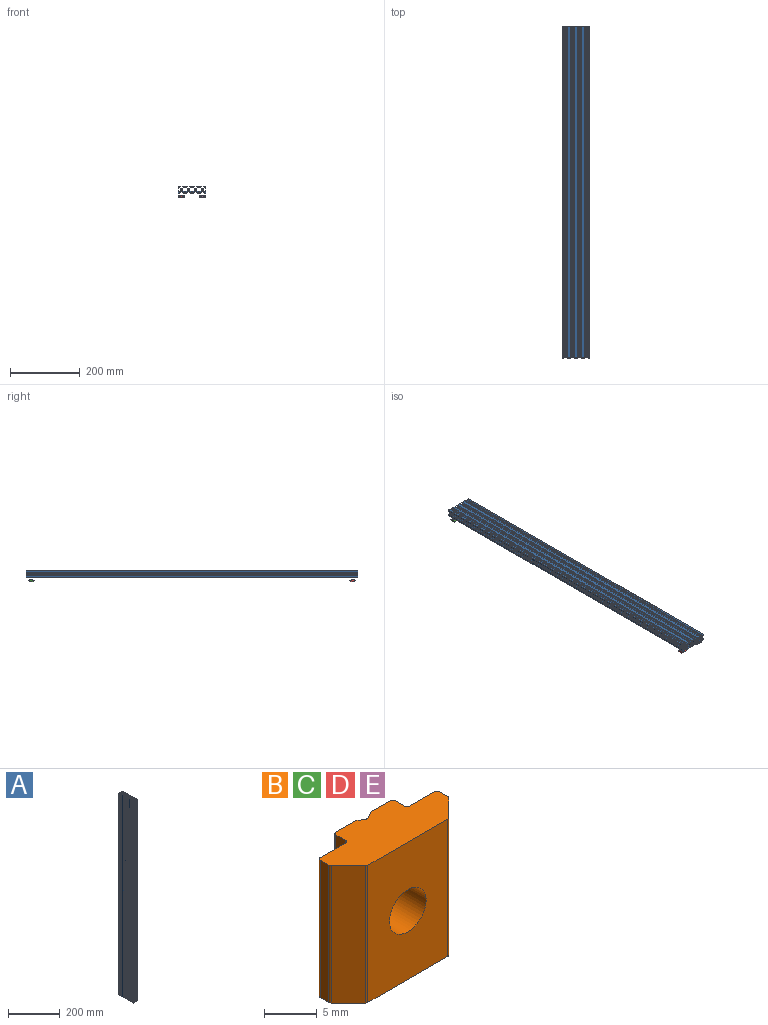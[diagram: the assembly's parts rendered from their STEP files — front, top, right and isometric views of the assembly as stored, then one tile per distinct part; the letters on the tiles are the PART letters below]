
ASSEMBLY  parts=5 mates=7
PART A: 240 faces, bbox 20x80x949 mm
  f0: plane 913.01x0.21mm, normal (0.71,0.71,0), area 271.1mm2, adj f2,f32,f234,f235
  f1: plane 12.01x0.21mm, normal (0.71,0.71,0), area 3.6mm2, adj f3,f33,f232,f234
  f2: plane 913.01x0.21mm, normal (0.71,-0.71,0), area 271.1mm2, adj f0,f4,f234,f235
  f3: plane 12.01x0.21mm, normal (0.71,-0.71,0), area 3.6mm2, adj f1,f5,f232,f234
  f4: plane 917.06x2.63mm, normal (1,0,0), area 2403.7mm2, adj f2,f48,f234,f235
  f5: plane 14.03x2.63mm, normal (1,0,0), area 33.1mm2, adj f3,f48,f232,f234
  f6: plane 917.06x2.63mm, normal (-1,0,0), area 2403.7mm2, adj f9,f77,f234,f235
  f7: plane 14.03x2.63mm, normal (-1,0,0), area 33.1mm2, adj f77,f79,f232,f234
  f8: plane 12.01x0.21mm, normal (-0.71,-0.71,0), area 3.6mm2, adj f10,f78,f233,f235
  f9: plane 913.01x0.21mm, normal (-0.71,-0.71,0), area 271.1mm2, adj f6,f11,f234,f235
  f10: plane 12.01x0.21mm, normal (-0.71,0.71,0), area 3.6mm2, adj f8,f81,f233,f235
  f11: plane 913.01x0.21mm, normal (-0.71,0.71,0), area 271.1mm2, adj f9,f12,f234,f235
  f12: plane 917.06x2.63mm, normal (-1,0,0), area 2403.7mm2, adj f11,f82,f234,f235
  f13: plane 14.03x2.63mm, normal (-1,0,0), area 33.1mm2, adj f80,f82,f232,f234
  f14: plane 14.03x2.63mm, normal (-1,0,0), area 33.1mm2, adj f122,f124,f232,f239
  f15: plane 917.06x2.63mm, normal (-1,0,0), area 2403.7mm2, adj f16,f122,f237,f239
  f16: plane 913.01x0.21mm, normal (-0.71,-0.71,0), area 271.1mm2, adj f15,f18,f237,f239
  f17: plane 12.01x0.21mm, normal (-0.71,-0.71,0), area 3.6mm2, adj f19,f123,f233,f237
  f18: plane 913.01x0.21mm, normal (-0.71,0.71,0), area 271.1mm2, adj f16,f21,f237,f239
  f19: plane 12.01x0.21mm, normal (-0.71,0.71,0), area 3.6mm2, adj f17,f126,f233,f237
  f20: plane 14.03x2.63mm, normal (-1,0,0), area 33.1mm2, adj f125,f127,f232,f239
  f21: plane 917.06x2.63mm, normal (-1,0,0), area 2403.7mm2, adj f18,f127,f237,f239
  f22: plane 14.03x2.63mm, normal (1,0,0), area 33.1mm2, adj f24,f156,f232,f239
  f23: plane 917.06x2.63mm, normal (1,0,0), area 2403.7mm2, adj f25,f156,f237,f239
  f24: plane 12.01x0.21mm, normal (0.71,0.71,0), area 3.6mm2, adj f22,f26,f232,f239
  f25: plane 913.01x0.21mm, normal (0.71,0.71,0), area 271.1mm2, adj f23,f27,f237,f239
  f26: plane 12.01x0.21mm, normal (0.71,-0.71,0), area 3.6mm2, adj f24,f28,f232,f239
  f27: plane 913.01x0.21mm, normal (0.71,-0.71,0), area 271.1mm2, adj f25,f29,f237,f239
  f28: plane 14.03x2.63mm, normal (1,0,0), area 33.1mm2, adj f26,f161,f232,f239
  f29: plane 917.06x2.63mm, normal (1,0,0), area 2403.7mm2, adj f27,f161,f237,f239
  f30: cylinder r=2.1mm len=12.86mm, axis (0,0,-1), area 163.8mm2, adj f232,f239
  f31: cylinder r=2.1mm len=12.86mm, axis (0,0,-1), area 163.8mm2, adj f232,f234
  f32: plane 917.06x2.63mm, normal (1,0,0), area 2403.7mm2, adj f0,f201,f234,f235
  f33: plane 14.03x2.63mm, normal (1,0,0), area 33.1mm2, adj f1,f201,f232,f234
  f34: plane 949x3.4mm, normal (0.71,-0.71,0), area 4563.1mm2, adj f35,f231,f232,f233
  f35: plane 949x5.68mm, normal (0,-1,0), area 5389.1mm2, adj f34,f36,f232,f233
  f36: plane 949x3.4mm, normal (-0.71,-0.71,0), area 4563.1mm2, adj f35,f37,f232,f233
  f37: plane 949x1.96mm, normal (0,-1,0), area 1860.7mm2, adj f36,f38,f232,f233
  f38: plane 949x5.4mm, normal (-1,0,0), area 5124.6mm2, adj f37,f39,f232,f233
  f39: plane 949x1.96mm, normal (0,1,0), area 1860.7mm2, adj f38,f40,f232,f233
  f40: plane 949x3.4mm, normal (-0.71,0.71,0), area 4563.1mm2, adj f39,f41,f232,f233
  f41: plane 949x5.68mm, normal (0,1,0), area 5389.1mm2, adj f40,f42,f232,f233
  f42: plane 949x3.4mm, normal (0.71,0.71,0), area 4563.1mm2, adj f41,f43,f232,f233
  f43: plane 949x1.96mm, normal (0,1,0), area 1860.7mm2, adj f42,f44,f232,f233
  f44: plane 949x5.4mm, normal (1,0,0), area 5124.6mm2, adj f43,f231,f232,f233
  f45: plane 12.01x0.21mm, normal (0.71,0.71,0), area 3.6mm2, adj f46,f228,f233,f235
  f46: plane 12.01x0.21mm, normal (0.71,-0.71,0), area 3.6mm2, adj f45,f47,f233,f235
  f47: plane 14.03x2.63mm, normal (1,0,0), area 33.1mm2, adj f46,f48,f233,f235
  f48: plane 949x2.66mm, normal (0.71,-0.71,0), area 3570.3mm2, adj f4,f5,f47,f49,f232,f233,f234,f235
  f49: plane 949x1.64mm, normal (0,-1,0), area 1555.7mm2, adj f48,f50,f232,f233
  f50: plane 949x2.38mm, normal (-1,0,0), area 2253.9mm2, adj f49,f51,f232,f233
  f51: plane 949x0.35mm, normal (0,-1,0), area 327.4mm2, adj f50,f52,f232,f233
  f52: plane 949x1.46mm, normal (0.71,-0.71,0), area 1952.7mm2, adj f51,f53,f232,f233
  f53: plane 949x4.92mm, normal (1,0,0), area 4669.1mm2, adj f52,f54,f232,f233
  f54: cylinder r=0.5mm len=949mm, axis (0,0,-1), area 745.3mm2, adj f53,f55,f232,f233
  f55: plane 949x4.92mm, normal (0,1,0), area 4669.1mm2, adj f54,f56,f232,f233
  f56: plane 949x1.46mm, normal (-0.71,0.71,0), area 1952.7mm2, adj f55,f57,f232,f233
  f57: plane 949x0.35mm, normal (-1,0,0), area 327.4mm2, adj f56,f58,f232,f233
  f58: plane 949x2.38mm, normal (0,-1,0), area 2253.9mm2, adj f57,f59,f232,f233
  f59: plane 949x1.64mm, normal (-1,0,0), area 1555.7mm2, adj f58,f60,f232,f233
  f60: plane 949x2.66mm, normal (-0.71,0.71,0), area 3570.8mm2, adj f59,f61,f232,f233
  f61: plane 949x2.63mm, normal (0,1,0), area 2495.2mm2, adj f60,f62,f232,f233
  f62: plane 949x0.21mm, normal (-0.71,0.71,0), area 281.8mm2, adj f61,f63,f232,f233
  f63: plane 949x0.21mm, normal (0.71,0.71,0), area 281.8mm2, adj f62,f64,f232,f233
  f64: plane 949x2.63mm, normal (0,1,0), area 2495.2mm2, adj f63,f65,f232,f233
  f65: plane 949x2.66mm, normal (0.71,0.71,0), area 3570.8mm2, adj f64,f66,f232,f233
  f66: plane 949x1.64mm, normal (1,0,0), area 1555.7mm2, adj f65,f67,f232,f233
  f67: plane 949x2.38mm, normal (0,-1,0), area 2253.9mm2, adj f66,f68,f232,f233
  f68: plane 949x0.35mm, normal (1,0,0), area 327.4mm2, adj f67,f69,f232,f233
  f69: plane 949x1.46mm, normal (0.71,0.71,0), area 1952.7mm2, adj f68,f70,f232,f233
  f70: plane 949x4.92mm, normal (0,1,0), area 4669.1mm2, adj f69,f71,f232,f233
  f71: cylinder r=0.5mm len=949mm, axis (0,0,-1), area 745.3mm2, adj f70,f72,f232,f233
  f72: plane 949x4.92mm, normal (-1,0,0), area 4669.1mm2, adj f71,f73,f232,f233
  f73: plane 949x1.46mm, normal (-0.71,-0.71,0), area 1952.7mm2, adj f72,f74,f232,f233
  f74: plane 949x0.35mm, normal (0,-1,0), area 327.4mm2, adj f73,f75,f232,f233
  f75: plane 949x2.38mm, normal (1,0,0), area 2253.9mm2, adj f74,f76,f232,f233
  f76: plane 949x1.64mm, normal (0,-1,0), area 1555.7mm2, adj f75,f77,f232,f233
  f77: plane 949x2.66mm, normal (-0.71,-0.71,0), area 3570.3mm2, adj f6,f7,f76,f78,f232,f233,f234,f235
  f78: plane 14.03x2.63mm, normal (-1,0,0), area 33.1mm2, adj f8,f77,f233,f235
  f79: plane 12.01x0.21mm, normal (-0.71,-0.71,0), area 3.6mm2, adj f7,f80,f232,f234
  f80: plane 12.01x0.21mm, normal (-0.71,0.71,0), area 3.6mm2, adj f13,f79,f232,f234
  f81: plane 14.03x2.63mm, normal (-1,0,0), area 33.1mm2, adj f10,f82,f233,f235
  f82: plane 949x2.66mm, normal (-0.71,0.71,0), area 3570.3mm2, adj f12,f13,f81,f83,f232,f233,f234,f235
  f83: plane 949x1.64mm, normal (0,1,0), area 1555.7mm2, adj f82,f84,f232,f233
  f84: plane 949x2.38mm, normal (1,0,0), area 2253.9mm2, adj f83,f85,f232,f233
  f85: plane 949x0.35mm, normal (0,1,0), area 327.4mm2, adj f84,f86,f232,f233
  f86: plane 949x1.46mm, normal (-0.71,0.71,0), area 1952.7mm2, adj f85,f87,f232,f233
  f87: plane 949x10.84mm, normal (-1,0,0), area 10287.2mm2, adj f86,f88,f232,f233
  f88: plane 949x1.46mm, normal (-0.71,-0.71,0), area 1952.7mm2, adj f87,f89,f232,f233
  f89: plane 949x0.35mm, normal (0,-1,0), area 327.4mm2, adj f88,f90,f232,f233
  f90: plane 949x2.38mm, normal (1,0,0), area 2253.9mm2, adj f89,f91,f232,f233
  f91: plane 949x1.64mm, normal (0,-1,0), area 1555.7mm2, adj f90,f92,f232,f233
  f92: plane 949x2.66mm, normal (-0.71,-0.71,0), area 3570.8mm2, adj f91,f93,f232,f233
  f93: plane 949x2.63mm, normal (-1,0,0), area 2495.2mm2, adj f92,f94,f232,f233
  f94: plane 949x0.21mm, normal (-0.71,-0.71,0), area 281.8mm2, adj f93,f95,f232,f233
  f95: plane 949x0.21mm, normal (-0.71,0.71,0), area 281.8mm2, adj f94,f96,f232,f233
  f96: plane 949x2.63mm, normal (-1,0,0), area 2495.2mm2, adj f95,f97,f232,f233
  f97: plane 949x2.66mm, normal (-0.71,0.71,0), area 3570.8mm2, adj f96,f98,f232,f233
  f98: plane 949x1.64mm, normal (0,1,0), area 1555.7mm2, adj f97,f99,f232,f233
  f99: plane 949x2.38mm, normal (1,0,0), area 2253.9mm2, adj f98,f100,f232,f233
  f100: plane 949x0.35mm, normal (0,1,0), area 327.4mm2, adj f99,f101,f232,f233
  f101: plane 949x1.46mm, normal (-0.71,0.71,0), area 1952.7mm2, adj f100,f102,f232,f233
  f102: plane 949x10.84mm, normal (-1,0,0), area 10287.2mm2, adj f101,f103,f232,f233
  f103: plane 949x1.46mm, normal (-0.71,-0.71,0), area 1952.7mm2, adj f102,f104,f232,f233
  f104: plane 949x0.35mm, normal (0,-1,0), area 327.4mm2, adj f103,f105,f232,f233
  f105: plane 949x2.38mm, normal (1,0,0), area 2253.9mm2, adj f104,f106,f232,f233
  f106: plane 949x1.64mm, normal (0,-1,0), area 1555.7mm2, adj f105,f107,f232,f233
  f107: plane 949x2.66mm, normal (-0.71,-0.71,0), area 3570.8mm2, adj f106,f108,f232,f233
  f108: plane 949x2.63mm, normal (-1,0,0), area 2495.2mm2, adj f107,f109,f232,f233
  f109: plane 949x0.21mm, normal (-0.71,-0.71,0), area 281.8mm2, adj f108,f110,f232,f233
  f110: plane 949x0.21mm, normal (-0.71,0.71,0), area 281.8mm2, adj f109,f111,f232,f233
  f111: plane 949x2.63mm, normal (-1,0,0), area 2495.2mm2, adj f110,f112,f232,f233
  f112: plane 949x2.66mm, normal (-0.71,0.71,0), area 3570.8mm2, adj f111,f113,f232,f233
  f113: plane 949x1.64mm, normal (0,1,0), area 1555.7mm2, adj f112,f114,f232,f233
  f114: plane 949x2.38mm, normal (1,0,0), area 2253.9mm2, adj f113,f115,f232,f233
  f115: plane 949x0.35mm, normal (0,1,0), area 327.4mm2, adj f114,f116,f232,f233
  f116: plane 949x1.46mm, normal (-0.71,0.71,0), area 1952.7mm2, adj f115,f117,f232,f233
  f117: plane 949x10.84mm, normal (-1,0,0), area 10287.2mm2, adj f116,f118,f232,f233
  f118: plane 949x1.46mm, normal (-0.71,-0.71,0), area 1952.7mm2, adj f117,f119,f232,f233
  f119: plane 949x0.35mm, normal (0,-1,0), area 327.4mm2, adj f118,f120,f232,f233
  f120: plane 949x2.38mm, normal (1,0,0), area 2253.9mm2, adj f119,f121,f232,f233
  f121: plane 949x1.64mm, normal (0,-1,0), area 1555.7mm2, adj f120,f122,f232,f233
  f122: plane 949x2.66mm, normal (-0.71,-0.71,0), area 3570.3mm2, adj f14,f15,f121,f123,f232,f233,f237,f239
  f123: plane 14.03x2.63mm, normal (-1,0,0), area 33.1mm2, adj f17,f122,f233,f237
  f124: plane 12.01x0.21mm, normal (-0.71,-0.71,0), area 3.6mm2, adj f14,f125,f232,f239
  f125: plane 12.01x0.21mm, normal (-0.71,0.71,0), area 3.6mm2, adj f20,f124,f232,f239
  f126: plane 14.03x2.63mm, normal (-1,0,0), area 33.1mm2, adj f19,f127,f233,f237
  f127: plane 949x2.66mm, normal (-0.71,0.71,0), area 3570.3mm2, adj f20,f21,f126,f128,f232,f233,f237,f239
  f128: plane 949x1.64mm, normal (0,1,0), area 1555.7mm2, adj f127,f129,f232,f233
  f129: plane 949x2.38mm, normal (1,0,0), area 2253.9mm2, adj f128,f130,f232,f233
  f130: plane 949x0.35mm, normal (0,1,0), area 327.4mm2, adj f129,f131,f232,f233
  f131: plane 949x1.46mm, normal (-0.71,0.71,0), area 1952.7mm2, adj f130,f132,f232,f233
  f132: plane 949x4.92mm, normal (-1,0,0), area 4669.1mm2, adj f131,f133,f232,f233
  f133: cylinder r=0.5mm len=949mm, axis (0,0,-1), area 745.3mm2, adj f132,f134,f232,f233
  f134: plane 949x4.92mm, normal (0,-1,0), area 4669.1mm2, adj f133,f135,f232,f233
  f135: plane 949x1.46mm, normal (0.71,-0.71,0), area 1952.7mm2, adj f134,f136,f232,f233
  f136: plane 949x0.35mm, normal (1,0,0), area 327.4mm2, adj f135,f137,f232,f233
  f137: plane 949x2.38mm, normal (0,1,0), area 2253.9mm2, adj f136,f138,f232,f233
  f138: plane 949x1.64mm, normal (1,0,0), area 1555.7mm2, adj f137,f139,f232,f233
  f139: plane 949x2.66mm, normal (0.71,-0.71,0), area 3570.8mm2, adj f138,f140,f232,f233
  f140: plane 949x2.63mm, normal (0,-1,0), area 2495.2mm2, adj f139,f141,f232,f233
  f141: plane 949x0.21mm, normal (0.71,-0.71,0), area 281.8mm2, adj f140,f142,f232,f233
  f142: plane 949x0.21mm, normal (-0.71,-0.71,0), area 281.8mm2, adj f141,f143,f232,f233
  f143: plane 949x2.63mm, normal (0,-1,0), area 2495.2mm2, adj f142,f144,f232,f233
  f144: plane 949x2.66mm, normal (-0.71,-0.71,0), area 3570.8mm2, adj f143,f145,f232,f233
  f145: plane 949x1.64mm, normal (-1,0,0), area 1555.7mm2, adj f144,f146,f232,f233
  f146: plane 949x2.38mm, normal (0,1,0), area 2253.9mm2, adj f145,f147,f232,f233
  f147: plane 949x0.35mm, normal (-1,0,0), area 327.4mm2, adj f146,f148,f232,f233
  f148: plane 949x1.46mm, normal (-0.71,-0.71,0), area 1952.7mm2, adj f147,f149,f232,f233
  f149: plane 949x4.92mm, normal (0,-1,0), area 4669.1mm2, adj f148,f150,f232,f233
  f150: cylinder r=0.5mm len=949mm, axis (0,0,-1), area 745.3mm2, adj f149,f151,f232,f233
  f151: plane 949x4.92mm, normal (1,0,0), area 4669.1mm2, adj f150,f152,f232,f233
  f152: plane 949x1.46mm, normal (0.71,0.71,0), area 1952.7mm2, adj f151,f153,f232,f233
  f153: plane 949x0.35mm, normal (0,1,0), area 327.4mm2, adj f152,f154,f232,f233
  f154: plane 949x2.38mm, normal (-1,0,0), area 2253.9mm2, adj f153,f155,f232,f233
  f155: plane 949x1.64mm, normal (0,1,0), area 1555.7mm2, adj f154,f156,f232,f233
  f156: plane 949x2.66mm, normal (0.71,0.71,0), area 3570.3mm2, adj f22,f23,f155,f157,f232,f233,f237,f239
  f157: plane 14.03x2.63mm, normal (1,0,0), area 33.1mm2, adj f156,f158,f233,f237
  f158: plane 12.01x0.21mm, normal (0.71,0.71,0), area 3.6mm2, adj f157,f159,f233,f237
  f159: plane 12.01x0.21mm, normal (0.71,-0.71,0), area 3.6mm2, adj f158,f160,f233,f237
  f160: plane 14.03x2.63mm, normal (1,0,0), area 33.1mm2, adj f159,f161,f233,f237
  f161: plane 949x2.66mm, normal (0.71,-0.71,0), area 3570.3mm2, adj f28,f29,f160,f162,f232,f233,f237,f239
  f162: plane 949x1.64mm, normal (0,-1,0), area 1555.7mm2, adj f161,f163,f232,f233
  f163: plane 949x2.38mm, normal (-1,0,0), area 2253.9mm2, adj f162,f164,f232,f233
  f164: plane 949x0.35mm, normal (0,-1,0), area 327.4mm2, adj f163,f165,f232,f233
  f165: plane 949x1.46mm, normal (0.71,-0.71,0), area 1952.7mm2, adj f164,f166,f232,f233
  f166: plane 949x10.84mm, normal (1,0,0), area 10287.2mm2, adj f165,f167,f232,f233
  f167: plane 949x1.46mm, normal (0.71,0.71,0), area 1952.7mm2, adj f166,f168,f232,f233
  f168: plane 949x0.35mm, normal (0,1,0), area 327.4mm2, adj f167,f169,f232,f233
  f169: plane 949x2.38mm, normal (-1,0,0), area 2253.9mm2, adj f168,f170,f232,f233
  f170: plane 949x1.64mm, normal (0,1,0), area 1555.7mm2, adj f169,f171,f232,f233
  f171: plane 949x2.66mm, normal (0.71,0.71,0), area 3570.8mm2, adj f170,f172,f232,f233
  f172: plane 949x2.63mm, normal (1,0,0), area 2495.2mm2, adj f171,f173,f232,f233
  f173: plane 949x0.21mm, normal (0.71,0.71,0), area 281.8mm2, adj f172,f174,f232,f233
  f174: plane 949x0.21mm, normal (0.71,-0.71,0), area 281.8mm2, adj f173,f175,f232,f233
  f175: plane 949x2.63mm, normal (1,0,0), area 2495.2mm2, adj f174,f176,f232,f233
  f176: plane 949x2.66mm, normal (0.71,-0.71,0), area 3570.8mm2, adj f175,f177,f232,f233
  f177: plane 949x1.64mm, normal (0,-1,0), area 1555.7mm2, adj f176,f178,f232,f233
  f178: plane 949x2.38mm, normal (-1,0,0), area 2253.9mm2, adj f177,f179,f232,f233
  f179: plane 949x0.35mm, normal (0,-1,0), area 327.4mm2, adj f178,f180,f232,f233
  f180: plane 949x1.46mm, normal (0.71,-0.71,0), area 1952.7mm2, adj f179,f181,f232,f233
  f181: plane 949x10.84mm, normal (1,0,0), area 10287.2mm2, adj f180,f182,f232,f233
  f182: plane 949x1.46mm, normal (0.71,0.71,0), area 1952.7mm2, adj f181,f183,f232,f233
  f183: plane 949x0.35mm, normal (0,1,0), area 327.4mm2, adj f182,f184,f232,f233
  f184: plane 949x2.38mm, normal (-1,0,0), area 2253.9mm2, adj f183,f185,f232,f233
  f185: plane 949x1.64mm, normal (0,1,0), area 1555.7mm2, adj f184,f186,f232,f233
  f186: plane 949x2.66mm, normal (0.71,0.71,0), area 3570.8mm2, adj f185,f187,f232,f233
  f187: plane 949x2.63mm, normal (1,0,0), area 2495.2mm2, adj f186,f188,f232,f233
  f188: plane 949x0.21mm, normal (0.71,0.71,0), area 281.8mm2, adj f187,f189,f232,f233
  f189: plane 949x0.21mm, normal (0.71,-0.71,0), area 281.8mm2, adj f188,f190,f232,f233
  f190: plane 949x2.63mm, normal (1,0,0), area 2495.2mm2, adj f189,f191,f232,f233
  f191: plane 949x2.66mm, normal (0.71,-0.71,0), area 3570.8mm2, adj f190,f192,f232,f233
  f192: plane 949x1.64mm, normal (0,-1,0), area 1555.7mm2, adj f191,f193,f232,f233
  f193: plane 949x2.38mm, normal (-1,0,0), area 2253.9mm2, adj f192,f194,f232,f233
  f194: plane 949x0.35mm, normal (0,-1,0), area 327.4mm2, adj f193,f195,f232,f233
  f195: plane 949x1.46mm, normal (0.71,-0.71,0), area 1952.7mm2, adj f194,f196,f232,f233
  f196: plane 949x10.84mm, normal (1,0,0), area 10287.2mm2, adj f195,f197,f232,f233
  f197: plane 949x1.46mm, normal (0.71,0.71,0), area 1952.7mm2, adj f196,f198,f232,f233
  f198: plane 949x0.35mm, normal (0,1,0), area 327.4mm2, adj f197,f199,f232,f233
  f199: plane 949x2.38mm, normal (-1,0,0), area 2253.9mm2, adj f198,f200,f232,f233
  f200: plane 949x1.64mm, normal (0,1,0), area 1555.7mm2, adj f199,f201,f232,f233
  f201: plane 949x2.66mm, normal (0.71,0.71,0), area 3570.3mm2, adj f32,f33,f200,f228,f232,f233,f234,f235
  f202: plane 949x3.4mm, normal (-0.71,-0.71,0), area 4563.1mm2, adj f203,f229,f232,f233
  f203: plane 949x1.96mm, normal (0,-1,0), area 1860.7mm2, adj f202,f204,f232,f233
  f204: plane 949x5.4mm, normal (-1,0,0), area 5124.6mm2, adj f203,f205,f232,f233
  f205: plane 949x1.96mm, normal (0,1,0), area 1860.7mm2, adj f204,f206,f232,f233
  f206: plane 949x3.4mm, normal (-0.71,0.71,0), area 4563.1mm2, adj f205,f207,f232,f233
  f207: plane 949x5.68mm, normal (0,1,0), area 5389.1mm2, adj f206,f208,f232,f233
  f208: plane 949x3.4mm, normal (0.71,0.71,0), area 4563.1mm2, adj f207,f209,f232,f233
  f209: plane 949x1.96mm, normal (0,1,0), area 1860.7mm2, adj f208,f210,f232,f233
  f210: plane 949x5.4mm, normal (1,0,0), area 5124.6mm2, adj f209,f211,f232,f233
  f211: plane 949x1.96mm, normal (0,-1,0), area 1860.7mm2, adj f210,f212,f232,f233
  f212: plane 949x3.4mm, normal (0.71,-0.71,0), area 4563.1mm2, adj f211,f229,f232,f233
  f213: plane 949x5.68mm, normal (0,1,0), area 5389.1mm2, adj f214,f230,f232,f233
  f214: plane 949x3.4mm, normal (0.71,0.71,0), area 4563.1mm2, adj f213,f215,f232,f233
  f215: plane 949x1.96mm, normal (0,1,0), area 1860.7mm2, adj f214,f216,f232,f233
  f216: plane 949x5.4mm, normal (1,0,0), area 5124.6mm2, adj f215,f217,f232,f233
  f217: plane 949x1.96mm, normal (0,-1,0), area 1860.7mm2, adj f216,f218,f232,f233
  f218: plane 949x3.4mm, normal (0.71,-0.71,0), area 4563.1mm2, adj f217,f219,f232,f233
  f219: plane 949x5.68mm, normal (0,-1,0), area 5389.1mm2, adj f218,f220,f232,f233
  f220: plane 949x3.4mm, normal (-0.71,-0.71,0), area 4563.1mm2, adj f219,f221,f232,f233
  f221: plane 949x1.96mm, normal (0,-1,0), area 1860.7mm2, adj f220,f222,f232,f233
  f222: plane 949x5.4mm, normal (-1,0,0), area 5124.6mm2, adj f221,f223,f232,f233
  f223: plane 949x1.96mm, normal (0,1,0), area 1860.7mm2, adj f222,f230,f232,f233
  f224: cylinder r=2.1mm len=949mm, axis (0,0,-1), area 12521.8mm2, adj f232,f233
  f225: cylinder r=2.1mm len=12.86mm, axis (0,0,-1), area 163.8mm2, adj f233,f237
  f226: cylinder r=2.1mm len=12.86mm, axis (0,0,-1), area 163.8mm2, adj f233,f235
  f227: cylinder r=2.1mm len=949mm, axis (0,0,-1), area 12521.8mm2, adj f232,f233
  f228: plane 14.03x2.63mm, normal (1,0,0), area 33.1mm2, adj f45,f201,f233,f235
  f229: plane 949x5.68mm, normal (0,-1,0), area 5389.1mm2, adj f202,f212,f232,f233
  f230: plane 949x3.4mm, normal (-0.71,0.71,0), area 4563.1mm2, adj f213,f223,f232,f233
  f231: plane 949x1.96mm, normal (0,-1,0), area 1860.7mm2, adj f34,f44,f232,f233
  f232: plane 80x20mm, normal (0,0,1), area 557.2mm2, adj f1,f3,f5,f7,f13,f14,f20,f22
  f233: plane 80x20mm, normal (0,0,-1), area 557.2mm2, adj f8,f10,f17,f19,f34,f35,f36,f37
  f234: cylinder r=3mm len=8.12mm, axis (-1,0,0), area 117.9mm2, adj f0,f1,f2,f3,f4,f5,f6,f7
  f235: cylinder r=3mm len=8.12mm, axis (-1,0,0), area 117.9mm2, adj f0,f2,f4,f6,f8,f9,f10,f11
  f236: cylinder r=2.1mm len=914.72mm, axis (0,0,-1), area 12057.6mm2, adj f234,f235
  f237: cylinder r=3mm len=8.12mm, axis (-1,0,0), area 117.9mm2, adj f15,f16,f17,f18,f19,f21,f23,f25
  f238: cylinder r=2.1mm len=914.72mm, axis (0,0,-1), area 12057.6mm2, adj f237,f239
  f239: cylinder r=3mm len=8.12mm, axis (-1,0,0), area 117.9mm2, adj f14,f15,f16,f18,f20,f21,f22,f23
PART B: 30 faces, bbox 16x6x16 mm
  f0: plane 16x6mm, normal (0,0,-1), area 73.9mm2, adj f1,f2,f3,f4,f5,f6,f7,f8
  f1: cylinder r=0.3mm len=16mm, axis (0,0,1), area 3.8mm2, adj f0,f2,f12,f13
  f2: plane 16x1.18mm, normal (-1,0,0), area 18.8mm2, adj f0,f1,f3,f13
  f3: cylinder r=0.3mm len=16mm, axis (0,0,1), area 7.5mm2, adj f0,f2,f4,f13
  f4: plane 16x3.4mm, normal (0,1,0), area 54.4mm2, adj f0,f3,f5,f13
  f5: cylinder r=0.3mm len=16mm, axis (0,0,1), area 7.5mm2, adj f0,f4,f6,f13
  f6: plane 16x1.3mm, normal (-1,0,0), area 20.8mm2, adj f0,f5,f7,f13
  f7: cylinder r=0.3mm len=16mm, axis (0,0,1), area 7.5mm2, adj f0,f6,f8,f13
  f8: plane 16x2.7mm, normal (0,1,0), area 38.5mm2, adj f0,f7,f9,f13,f14,f15
  f9: cylinder r=2.46mm len=6mm, axis (0,-1,0), area 91.6mm2, adj f8,f10,f14,f15,f16,f17,f18,f19
  f10: plane 16x10.75mm, normal (0,-1,0), area 153mm2, adj f0,f9,f11,f13,f29
  f11: cylinder r=0.3mm len=16mm, axis (0,0,1), area 3.8mm2, adj f0,f10,f12,f13
  f12: plane 16x2.32mm, normal (-0.71,-0.71,0), area 52.6mm2, adj f0,f1,f11,f13
  f13: plane 16x6mm, normal (0,0,1), area 73.9mm2, adj f1,f2,f3,f4,f5,f6,f7,f8
  f14: plane 5.76x0.86mm, normal (0.5,0.87,0), area 5.5mm2, adj f0,f8,f9,f16
  f15: plane 5.76x0.86mm, normal (0.5,0.87,0), area 5.5mm2, adj f8,f9,f13,f17
  f16: cylinder r=0.3mm len=5.54mm, axis (0,0,1), area 1.7mm2, adj f0,f9,f14,f18
  f17: cylinder r=0.3mm len=5.54mm, axis (0,0,1), area 1.7mm2, adj f9,f13,f15,f19
  f18: plane 5.76x0.86mm, normal (-0.5,0.87,0), area 5.5mm2, adj f0,f9,f16,f20
  f19: plane 5.76x0.86mm, normal (-0.5,0.87,0), area 5.5mm2, adj f9,f13,f17,f20
  f20: plane 16x2.7mm, normal (0,1,0), area 38.5mm2, adj f0,f9,f13,f18,f19,f21
  f21: cylinder r=0.3mm len=16mm, axis (0,0,1), area 7.5mm2, adj f0,f13,f20,f22
  f22: plane 16x1.3mm, normal (1,0,0), area 20.8mm2, adj f0,f13,f21,f23
  f23: cylinder r=0.3mm len=16mm, axis (0,0,1), area 7.5mm2, adj f0,f13,f22,f24
  f24: plane 16x3.4mm, normal (0,1,0), area 54.4mm2, adj f0,f13,f23,f25
  f25: cylinder r=0.3mm len=16mm, axis (0,0,1), area 7.5mm2, adj f0,f13,f24,f26
  f26: plane 16x1.18mm, normal (1,0,0), area 18.8mm2, adj f0,f13,f25,f27
  f27: cylinder r=0.3mm len=16mm, axis (0,0,1), area 3.8mm2, adj f0,f13,f26,f28
  f28: plane 16x2.32mm, normal (0.71,-0.71,0), area 52.6mm2, adj f0,f13,f27,f29
  f29: cylinder r=0.3mm len=16mm, axis (0,0,1), area 3.8mm2, adj f0,f10,f13,f28
PART C: same geometry as B
PART D: same geometry as B
PART E: same geometry as B
PLACE A rot(axis=(-0.58,-0.58,-0.58),120deg) t=(1641.22,-989.34,35)mm
PLACE B rot(axis=(0.58,0.58,0.58),120deg) t=(1633.22,-55.34,18.19)mm
PLACE C rot(axis=(0.58,0.58,0.58),120deg) t=(1573.22,-55.34,18.19)mm
PLACE D rot(axis=(0.58,0.58,0.58),120deg) t=(1573.22,-974.34,18.19)mm
PLACE E rot(axis=(0.58,0.58,0.58),120deg) t=(1633.22,-974.34,18.19)mm
MATE slider E.f9 <-> A.f235  axis (0,0,-1) through (1641.22,-974.34,12.19)mm
MATE planar D.f9 <-> C.f9  axis (0,0,-1) through (1581.22,-974.34,12.19)mm
MATE planar D.f9 <-> E.f9  axis (0,0,-1) through (1581.22,-974.34,12.19)mm
MATE planar B.f9 <-> C.f9  axis (0,0,-1) through (1641.22,-55.34,12.19)mm
MATE slider B.f9 <-> A.f234  axis (0,0,-1) through (1641.22,-55.34,12.19)mm
MATE slider C.f9 <-> A.f239  axis (0,0,-1) through (1581.22,-55.34,12.19)mm
MATE slider D.f9 <-> A.f237  axis (0,0,-1) through (1581.22,-974.34,12.19)mm
